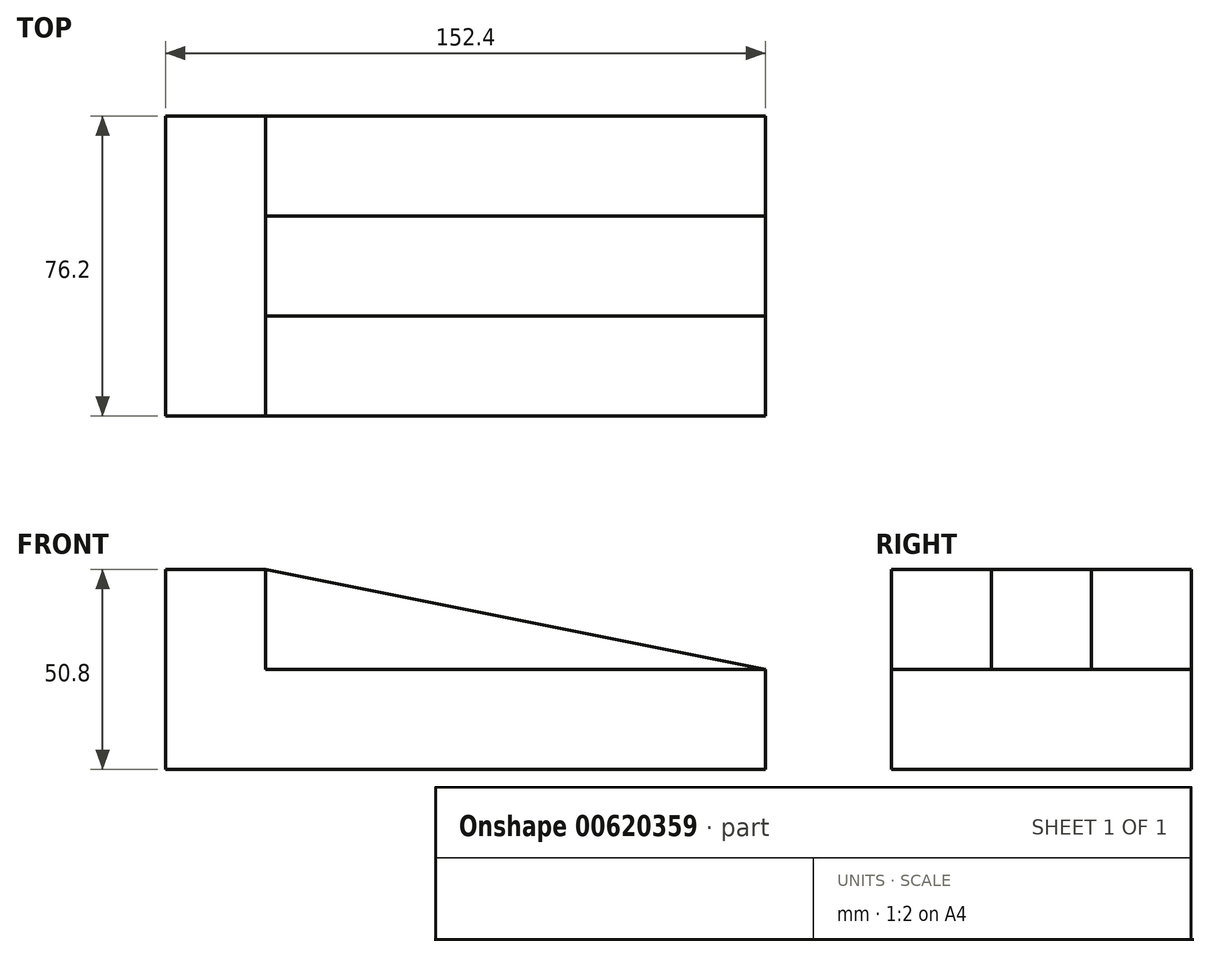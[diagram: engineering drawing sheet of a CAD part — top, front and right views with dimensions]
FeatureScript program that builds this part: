
annotation { "Feature Type Name" : "Feature", "Feature Type Description" : "" }
export const myFeature = defineFeature(function(context is Context, id is Id, definition is map)
    precondition{}
    {
        {
            var Q0;
            Q0=qCreatedBy(makeId("Front.planeOp"),FACE);
            var sketch = newSketch(context, id + "F0", { "sketchPlane" : qUnion([Q0])});
            skLineSegment(sketch, "E0", {"start": v(0, 0) * mm, "end": v(0, 50.8) * mm});
            skLineSegment(sketch, "E1", {"start": v(0, 50.8) * mm, "end": v(25.4, 50.8) * mm});
            skLineSegment(sketch, "E2", {"start": v(25.4, 50.8) * mm, "end": v(25.4, 25.4) * mm});
            skLineSegment(sketch, "E3", {"start": v(25.4, 25.4) * mm, "end": v(152.4, 25.4) * mm});
            skLineSegment(sketch, "E4", {"start": v(152.4, 25.4) * mm, "end": v(152.4, 0) * mm});
            skLineSegment(sketch, "E5", {"start": v(152.4, 0) * mm, "end": v(0, 0) * mm});
            skSolve(sketch);
        }
        {
            var Q0;
            Q0 = qSketchRegion(id + "F0", true);
            extrude(context, id + "F1", {"entities" : qUnion([Q0]), "depth" : 76.2 * mm, "offsetDistance" : 25.4 * mm});
        }
        {
            var Q0;
            Q0=makeQuery(id+"F1.opExtrude","SWEPT_FACE",FACE,{"disambiguationData":[OSD([sQuery(id+"F0.wireOp",EDGE,"E2")])]});
            var sketch = newSketch(context, id + "F2", { "sketchPlane" : qUnion([Q0])});
            skLineSegment(sketch, "E6", {"start": v(-50.8, 50.8) * mm, "end": v(-50.8, 25.4) * mm});
            skLineSegment(sketch, "E7", {"start": v(-50.8, 25.4) * mm, "end": v(-25.4, 25.4) * mm});
            skLineSegment(sketch, "E8", {"start": v(-25.4, 25.4) * mm, "end": v(-25.4, 50.8) * mm});
            skLineSegment(sketch, "E9", {"start": v(-25.4, 50.8) * mm, "end": v(-50.8, 50.8) * mm});
            skSolve(sketch);
        }
        {
            var Q0;
            Q0=makeQuery(id+"F2.imprint","IMPRINT",FACE,{"disambiguationData":[TD([[makeQuery(id+"F2.imprint","IMPRINT",EDGE,{"derivedFrom":sQuery(id+"F2.wireOp",EDGE,"E6")}),1.0]])]});
            extrude(context, id + "F3", {"entities" : qUnion([Q0]), "operationType" : NewBodyOperationType.ADD, "depth" : 127 * mm, "offsetDistance" : 25.4 * mm});
        }
        {
            var Q0;
            Q0=makeQuery(id+"F3.opExtrude","SWEPT_FACE",FACE,{"disambiguationData":[OSD([sQuery(id+"F2.wireOp",EDGE,"E8")])]});
            var sketch = newSketch(context, id + "F4", { "sketchPlane" : qUnion([Q0])});
            skLineSegment(sketch, "E10", {"start": v(-25.4, 50.8) * mm, "end": v(-152.4, 25.4) * mm});
            skLineSegment(sketch, "E11", {"start": v(-152.4, 25.4) * mm, "end": v(-152.4, 50.8) * mm});
            skLineSegment(sketch, "E12", {"start": v(-152.4, 50.8) * mm, "end": v(-25.4, 50.8) * mm});
            skSolve(sketch);
        }
        {
            var Q0;
            Q0=makeQuery(id+"F4.imprint","IMPRINT",FACE,{"disambiguationData":[TD([[makeQuery(id+"F4.imprint","IMPRINT",EDGE,{"derivedFrom":sQuery(id+"F4.wireOp",EDGE,"E10")}),-1.0]])]});
            extrude(context, id + "F5", {"entities" : qUnion([Q0]), "operationType" : NewBodyOperationType.REMOVE, "oppositeDirection" : true, "depth" : 127 * mm, "offsetDistance" : 25.4 * mm});
        }
    });
